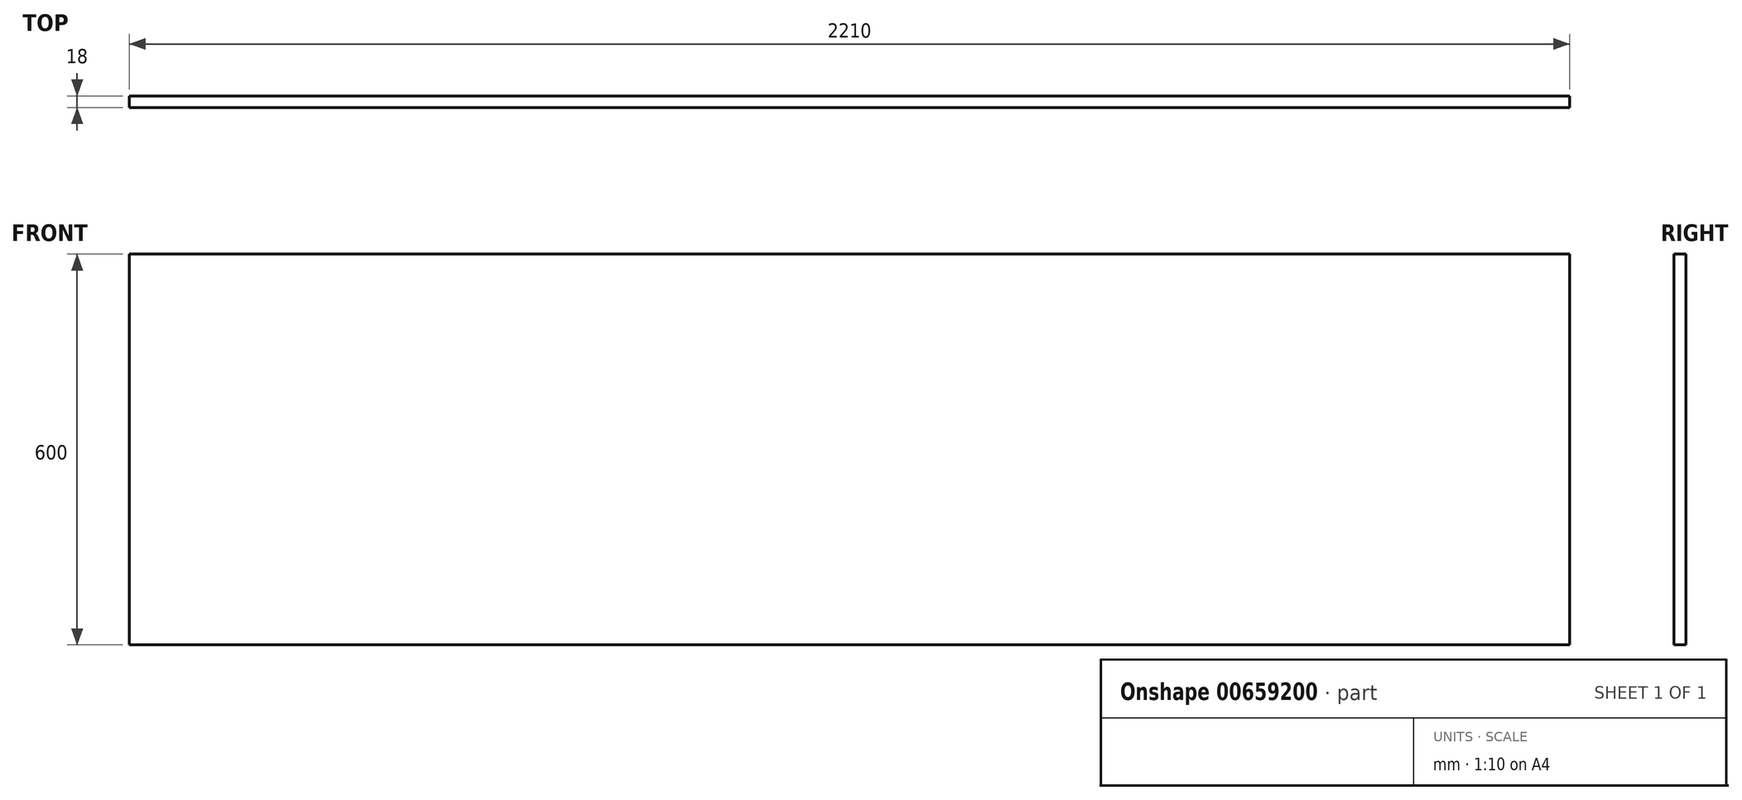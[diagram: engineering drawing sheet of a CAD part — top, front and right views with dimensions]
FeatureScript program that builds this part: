
annotation { "Feature Type Name" : "Feature", "Feature Type Description" : "" }
export const myFeature = defineFeature(function(context is Context, id is Id, definition is map)
    precondition{}
    {
        {
            var Q0;
            Q0=qCreatedBy(makeId("Front.planeOp"),FACE);
            var sketch = newSketch(context, id + "F0", { "sketchPlane" : qUnion([Q0])});
            skLineSegment(sketch, "E0.bottom", {"start": v(-1104.11, -32.12) * mm, "end": v(1105.89, -32.12) * mm});
            skLineSegment(sketch, "E0.top", {"start": v(-1104.11, -632.12) * mm, "end": v(1105.89, -632.12) * mm});
            skLineSegment(sketch, "E0.left", {"start": v(-1104.11, -32.12) * mm, "end": v(-1104.11, -632.12) * mm});
            skLineSegment(sketch, "E0.right", {"start": v(1105.89, -32.12) * mm, "end": v(1105.89, -632.12) * mm});
            skSolve(sketch);
        }
        {
            var Q0;
            Q0=makeQuery(id+"F0.imprint","IMPRINT",FACE,{"disambiguationData":[TD([[makeQuery(id+"F0.imprint","IMPRINT",EDGE,{"derivedFrom":sQuery(id+"F0.wireOp",EDGE,"E0.bottom")}),-1.0]])]});
            extrude(context, id + "F1", {"entities" : qUnion([Q0]), "endBound" : BoundingType.SYMMETRIC, "depth" : 18 * mm, "offsetDistance" : 25 * mm});
        }
    });
